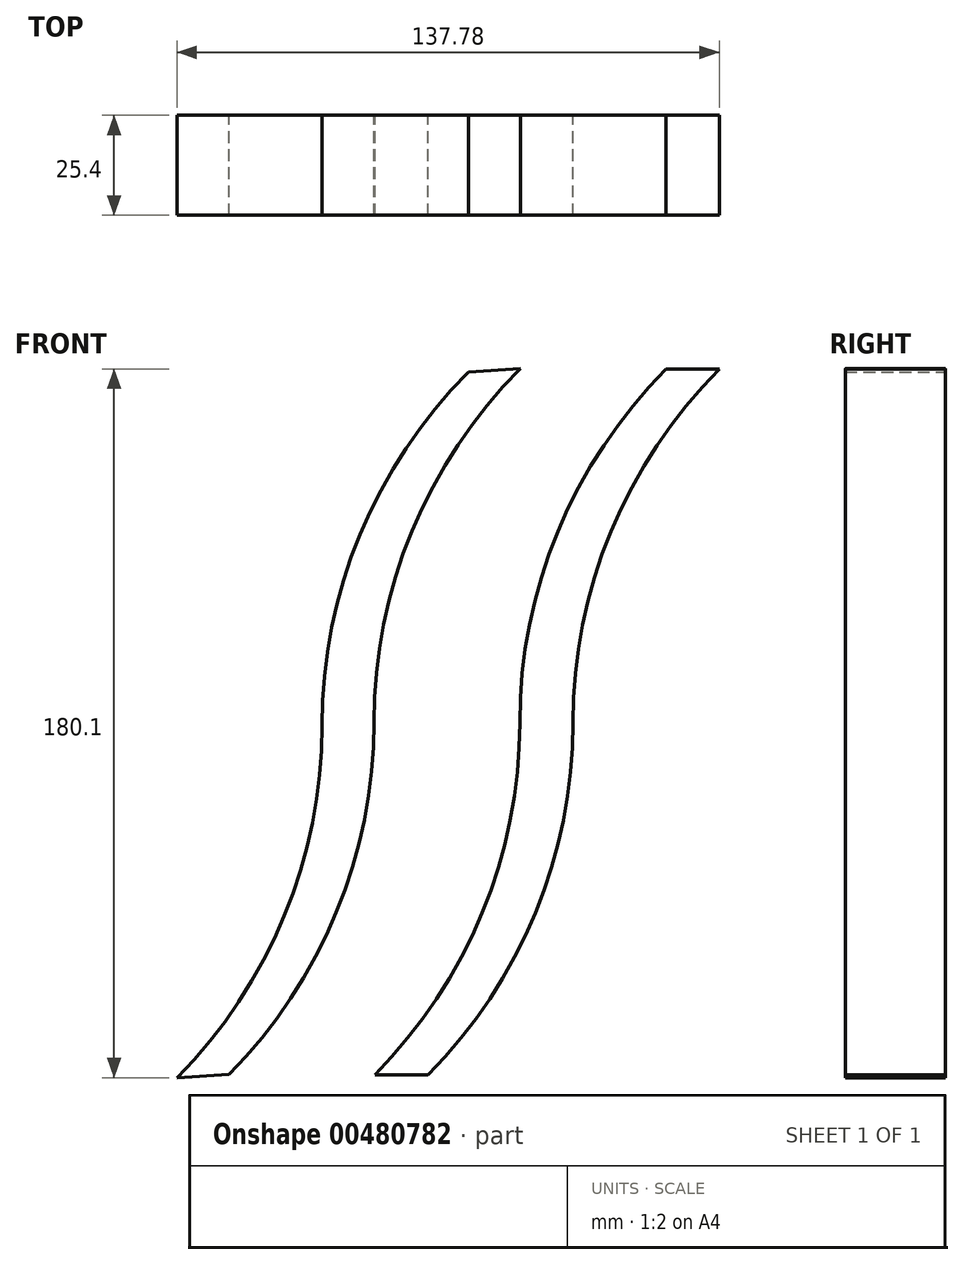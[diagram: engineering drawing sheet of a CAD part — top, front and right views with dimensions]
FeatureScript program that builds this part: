
annotation { "Feature Type Name" : "Feature", "Feature Type Description" : "" }
export const myFeature = defineFeature(function(context is Context, id is Id, definition is map)
    precondition{}
    {
        {
            var Q0;
            Q0=qCreatedBy(makeId("Front.planeOp"),FACE);
            var sketch = newSketch(context, id + "F0", { "sketchPlane" : qUnion([Q0])});
            skArc(sketch, "E0", {"start": v(-55.69, -89.18) * mm, "mid": v(-28.43, -48.1) * mm, "end": v(-18.86, 0.25) * mm});
            skArc(sketch, "E1", {"start": v(18.33, 90.05) * mm, "mid": v(-9.2, 48.85) * mm, "end": v(-18.86, 0.25) * mm});
            skArc(sketch, "E2", {"start": v(-18.63, -89.3) * mm, "mid": v(8.63, -48.23) * mm, "end": v(18.2, 0.13) * mm});
            skArc(sketch, "E3", {"start": v(55.39, 89.93) * mm, "mid": v(27.86, 48.73) * mm, "end": v(18.2, 0.13) * mm});
            skArc(sketch, "E4", {"start": v(-68.9, -90.05) * mm, "mid": v(-41.64, -48.98) * mm, "end": v(-32.07, -0.63) * mm});
            skArc(sketch, "E5", {"start": v(5.13, 89.18) * mm, "mid": v(-22.4, 47.98) * mm, "end": v(-32.07, -0.63) * mm});
            skArc(sketch, "E6", {"start": v(-5.13, -89.3) * mm, "mid": v(22.13, -48.23) * mm, "end": v(31.7, 0.13) * mm});
            skArc(sketch, "E7", {"start": v(68.9, 89.93) * mm, "mid": v(41.36, 48.73) * mm, "end": v(31.7, 0.13) * mm});
            skLineSegment(sketch, "E8", {"start": v(-68.9, -90.05) * mm, "end": v(-55.69, -89.18) * mm});
            skLineSegment(sketch, "E9", {"start": v(-18.63, -89.3) * mm, "end": v(-5.13, -89.3) * mm});
            skLineSegment(sketch, "E10", {"start": v(-55.69, -89.18) * mm, "end": v(-18.63, -89.3) * mm});
            skLineSegment(sketch, "E11", {"start": v(5.13, 89.18) * mm, "end": v(18.33, 90.05) * mm});
            skLineSegment(sketch, "E12", {"start": v(18.33, 90.05) * mm, "end": v(55.39, 89.93) * mm});
            skLineSegment(sketch, "E13", {"start": v(55.39, 89.93) * mm, "end": v(68.9, 89.93) * mm});
            skSolve(sketch);
        }
        {
            var Q0;
            Q0=makeQuery(id+"F0.imprint","IMPRINT",FACE,{"disambiguationData":[TD([[makeQuery(id+"F0.imprint","IMPRINT",EDGE,{"derivedFrom":sQuery(id+"F0.wireOp",EDGE,"E0")}),1.0]])]});
            var Q1;
            Q1=makeQuery(id+"F0.imprint","IMPRINT",FACE,{"disambiguationData":[TD([[makeQuery(id+"F0.imprint","IMPRINT",EDGE,{"derivedFrom":sQuery(id+"F0.wireOp",EDGE,"E2")}),-1.0]])]});
            extrude(context, id + "F1", {"entities" : qUnion([Q0, Q1]), "depth" : 25.4 * mm});
        }
    });
